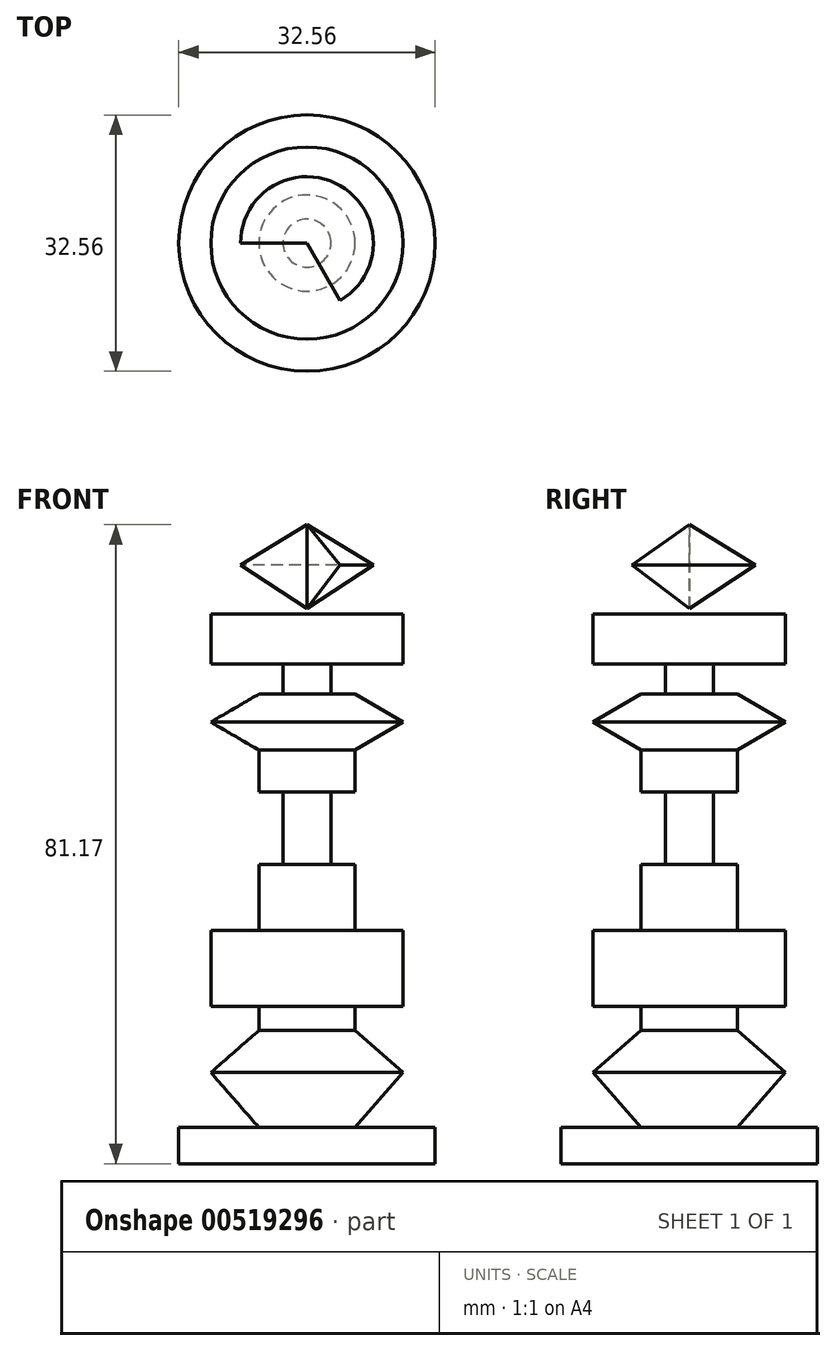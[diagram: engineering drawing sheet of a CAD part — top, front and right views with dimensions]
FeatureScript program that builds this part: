
annotation { "Feature Type Name" : "Feature", "Feature Type Description" : "" }
export const myFeature = defineFeature(function(context is Context, id is Id, definition is map)
    precondition{}
    {
        {
            var Q0;
            Q0=qCreatedBy(makeId("Front.planeOp"),FACE);
            var sketch = newSketch(context, id + "F0", { "sketchPlane" : qUnion([Q0])});
            skLineSegment(sketch, "E0", {"start": v(0, 69.83) * mm, "end": v(-12.21, 69.83) * mm});
            skLineSegment(sketch, "E1", {"start": v(-12.21, 69.83) * mm, "end": v(-12.21, 63.47) * mm});
            skLineSegment(sketch, "E2", {"start": v(-12.21, 63.47) * mm, "end": v(-3.05, 63.47) * mm});
            skLineSegment(sketch, "E3", {"start": v(-3.05, 63.47) * mm, "end": v(-3.05, 59.66) * mm});
            skLineSegment(sketch, "E4", {"start": v(-3.05, 59.66) * mm, "end": v(-6.1, 59.66) * mm});
            skLineSegment(sketch, "E5", {"start": v(-6.1, 59.66) * mm, "end": v(-12.21, 56.1) * mm});
            skLineSegment(sketch, "E6", {"start": v(-12.21, 56.1) * mm, "end": v(-6.1, 52.53) * mm});
            skLineSegment(sketch, "E7", {"start": v(-6.1, 52.53) * mm, "end": v(-6.1, 47.2) * mm});
            skLineSegment(sketch, "E8", {"start": v(-3.05, 47.2) * mm, "end": v(-6.1, 47.2) * mm});
            skLineSegment(sketch, "E9", {"start": v(-3.05, 47.2) * mm, "end": v(-3.05, 38.03) * mm});
            skLineSegment(sketch, "E10", {"start": v(-3.05, 38.03) * mm, "end": v(-6.1, 38.03) * mm});
            skLineSegment(sketch, "E11", {"start": v(-6.1, 38.03) * mm, "end": v(-6.1, 29.64) * mm});
            skLineSegment(sketch, "E12", {"start": v(-6.1, 29.64) * mm, "end": v(-12.21, 29.64) * mm});
            skLineSegment(sketch, "E13", {"start": v(-12.21, 29.64) * mm, "end": v(-12.21, 19.97) * mm});
            skLineSegment(sketch, "E14", {"start": v(-12.21, 19.97) * mm, "end": v(-6.1, 19.97) * mm});
            skLineSegment(sketch, "E15", {"start": v(-6.1, 19.97) * mm, "end": v(-6.1, 16.92) * mm});
            skLineSegment(sketch, "E16", {"start": v(-6.1, 16.92) * mm, "end": v(-12.21, 11.58) * mm});
            skLineSegment(sketch, "E17", {"start": v(-12.21, 11.58) * mm, "end": v(-6.1, 4.6) * mm});
            skLineSegment(sketch, "E18", {"start": v(-16.28, 4.6) * mm, "end": v(-16.28, 0) * mm});
            skLineSegment(sketch, "E19", {"start": v(-16.28, 0) * mm, "end": v(-16.28, 4.6) * mm});
            skLineSegment(sketch, "E20", {"start": v(-6.1, 4.6) * mm, "end": v(-16.28, 4.6) * mm});
            skLineSegment(sketch, "E21", {"start": v(-16.28, 0) * mm, "end": v(0, 0) * mm});
            skLineSegment(sketch, "E22", {"start": v(0, 0) * mm, "end": v(0, 69.83) * mm});
            skSolve(sketch);
        }
        {
            var Q0;
            Q0=makeQuery(id+"F0.imprint","IMPRINT",FACE,{"disambiguationData":[TD([[makeQuery(id+"F0.imprint","IMPRINT",EDGE,{"derivedFrom":sQuery(id+"F0.wireOp",EDGE,"E0")}),1.0]])]});
            var Q1;
            Q1=sQuery(id+"F0.wireOp",EDGE,"E22");
            revolve(context, id + "F1", {"entities" : qUnion([Q0]), "axis" : qUnion([Q1]), "revolveType" : RevolveType.FULL});
        }
        {
            var Q0;
            Q0=qCreatedBy(makeId("Front.planeOp"),FACE);
            var sketch = newSketch(context, id + "F2", { "sketchPlane" : qUnion([Q0])});
            skLineSegment(sketch, "E23", {"start": v(0, 70.52) * mm, "end": v(-8.44, 76.05) * mm});
            skLineSegment(sketch, "E24", {"start": v(-8.44, 76.05) * mm, "end": v(0, 81.17) * mm});
            skLineSegment(sketch, "E25", {"start": v(0, 81.17) * mm, "end": v(0, 70.52) * mm});
            skSolve(sketch);
        }
        {
            var Q0;
            Q0=makeQuery(id+"F2.imprint","IMPRINT",FACE,{"disambiguationData":[TD([[makeQuery(id+"F2.imprint","IMPRINT",EDGE,{"derivedFrom":sQuery(id+"F2.wireOp",EDGE,"E23")}),-1.0]])]});
            var Q1;
            Q1=sQuery(id+"F2.wireOp",EDGE,"E25");
            revolve(context, id + "F3", {"entities" : qUnion([Q0]), "axis" : qUnion([Q1]), "revolveType" : RevolveType.ONE_DIRECTION, "angle" : 240 * degree});
        }
    });
